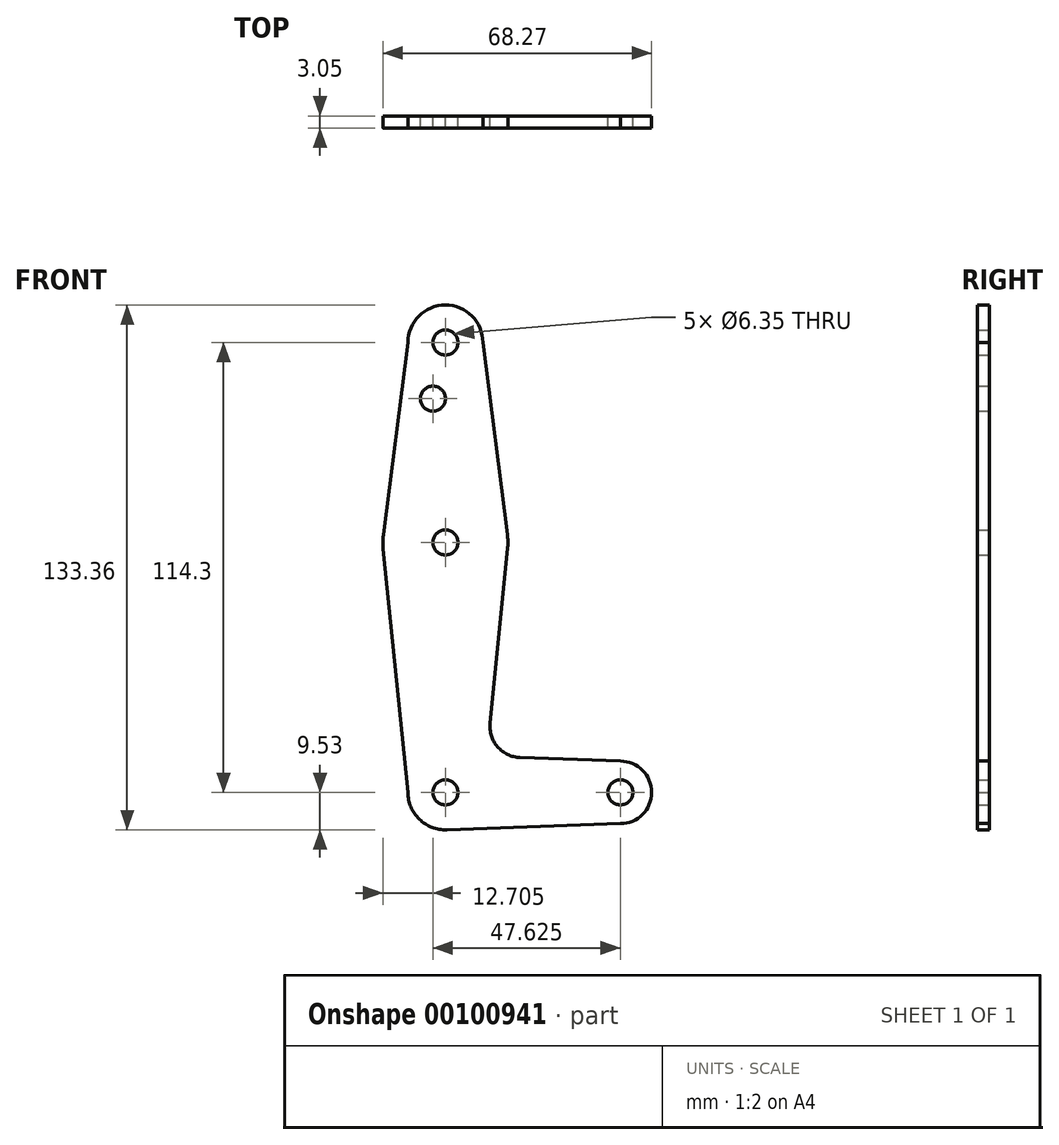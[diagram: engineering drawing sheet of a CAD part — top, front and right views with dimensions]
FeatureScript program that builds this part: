
annotation { "Feature Type Name" : "Feature", "Feature Type Description" : "" }
export const myFeature = defineFeature(function(context is Context, id is Id, definition is map)
    precondition{}
    {
        {
            var Q0;
            Q0=qCreatedBy(makeId("Front.planeOp"),FACE);
            var sketch = newSketch(context, id + "F0", { "sketchPlane" : qUnion([Q0])});
            skLineSegment(sketch, "E0", {"start": v(0, 114.3) * mm, "end": v(0, 0) * mm, "construction": true});
            skLineSegment(sketch, "E1", {"start": v(0, 0) * mm, "end": v(44.45, 0) * mm, "construction": true});
            skCircle(sketch, "E2", {"center": v(0, 114.3) * mm, "radius": 9.53 * mm});
            skCircle(sketch, "E3", {"center": v(0, 63.5) * mm, "radius": 15.88 * mm});
            skCircle(sketch, "E4", {"center": v(0, 0) * mm, "radius": 9.53 * mm});
            skCircle(sketch, "E5", {"center": v(44.45, 0) * mm, "radius": 7.94 * mm});
            skLineSegment(sketch, "E6", {"start": v(-15.75, 65.5) * mm, "end": v(-9.53, 114.3) * mm});
            skLineSegment(sketch, "E7", {"start": v(15.75, 65.5) * mm, "end": v(9.53, 114.3) * mm});
            skLineSegment(sketch, "E8", {"start": v(-15.8, 61.9) * mm, "end": v(-9.52, 0) * mm});
            skLineSegment(sketch, "E9", {"start": v(15.8, 61.91) * mm, "end": v(11.34, 17.6) * mm});
            skLineSegment(sketch, "E10", {"start": v(18.97, 8.85) * mm, "end": v(44.45, 7.94) * mm});
            skLineSegment(sketch, "E11", {"start": v(0.34, -9.52) * mm, "end": v(44.45, -7.94) * mm});
            skCircle(sketch, "E12", {"center": v(0, 114.3) * mm, "radius": 3.18 * mm});
            skCircle(sketch, "E13", {"center": v(0, 63.5) * mm, "radius": 3.18 * mm});
            skCircle(sketch, "E14", {"center": v(0, 0) * mm, "radius": 3.18 * mm});
            skCircle(sketch, "E15", {"center": v(44.45, 0) * mm, "radius": 3.18 * mm});
            skCircle(sketch, "E16", {"center": v(-3.18, 100.03) * mm, "radius": 3.18 * mm});
            skPoint(sketch, "E17.newPointB", {"position": v(9.57, 0) * mm});
            skArc(sketch, "E17.filletArc", {"start": v(11.34, 17.6) * mm, "mid": v(13.26, 11.57) * mm, "end": v(18.97, 8.85) * mm});
            skSolve(sketch);
        }
        {
            var Q0;
            Q0=makeQuery(id+"F0.imprint","IMPRINT",FACE,{"disambiguationData":[TD([[makeQuery(id+"F0.imprint","IMPRINT",EDGE,{"derivedFrom":sQuery(id+"F0.wireOp",EDGE,"E13")}),-1.0]])]});
            var Q1;
            {var subQ0=sQuery(id+"F0.wireOp",EDGE,"E8");Q1=makeQuery(id+"F0.imprint","IMPRINT",FACE,{"disambiguationData":[TD([[makeQuery(id+"F0.imprint","IMPRINT",EDGE,{"derivedFrom":subQ0}),1.0]])]});}
            var Q2;
            Q2=makeQuery(id+"F0.imprint","IMPRINT",FACE,{"disambiguationData":[TD([[makeQuery(id+"F0.imprint","IMPRINT",EDGE,{"derivedFrom":sQuery(id+"F0.wireOp",EDGE,"E14")}),-1.0]])]});
            var Q3;
            {var subQ1=sQuery(id+"F0.wireOp",EDGE,"E6");Q3=makeQuery(id+"F0.imprint","IMPRINT",FACE,{"disambiguationData":[TD([[makeQuery(id+"F0.imprint","IMPRINT",EDGE,{"derivedFrom":subQ1}),-1.0]])]});}
            var Q4;
            Q4=makeQuery(id+"F0.imprint","IMPRINT",FACE,{"disambiguationData":[TD([[makeQuery(id+"F0.imprint","IMPRINT",EDGE,{"derivedFrom":sQuery(id+"F0.wireOp",EDGE,"E12")}),-1.0]])]});
            var Q5;
            Q5=makeQuery(id+"F0.imprint","IMPRINT",FACE,{"disambiguationData":[TD([[makeQuery(id+"F0.imprint","IMPRINT",EDGE,{"derivedFrom":sQuery(id+"F0.wireOp",EDGE,"E15")}),-1.0]])]});
            extrude(context, id + "F1", {"entities" : qUnion([Q0, Q1, Q2, Q3, Q4, Q5]), "depth" : 3.05 * mm});
        }
    });
